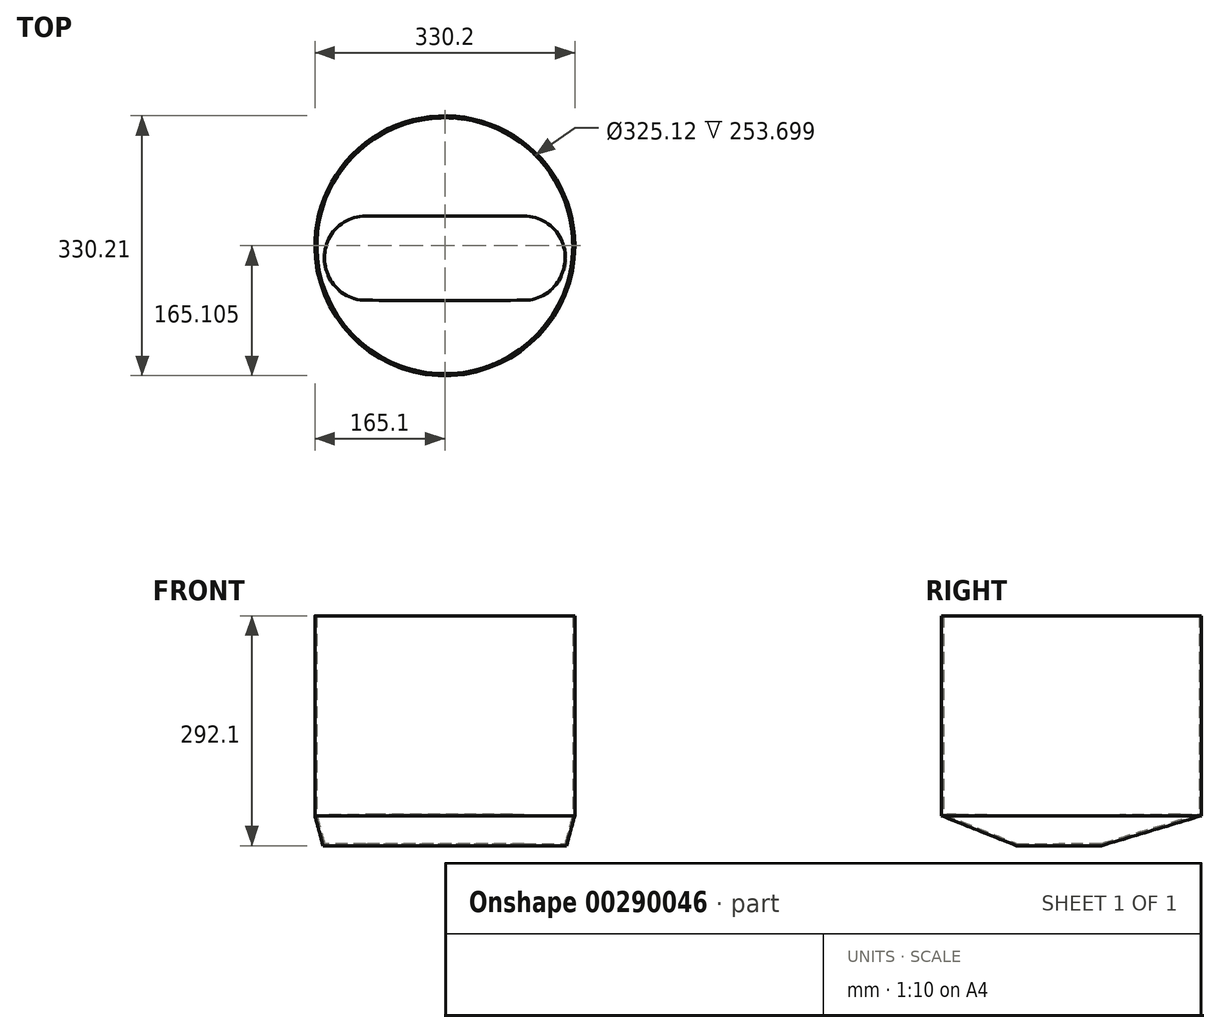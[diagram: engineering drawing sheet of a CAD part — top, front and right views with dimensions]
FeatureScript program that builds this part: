
annotation { "Feature Type Name" : "Feature", "Feature Type Description" : "" }
export const myFeature = defineFeature(function(context is Context, id is Id, definition is map)
    precondition{}
    {
        {
            var Q0;
            Q0=qCreatedBy(makeId("Top.planeOp"),FACE);
            var sketch = newSketch(context, id + "F0", { "sketchPlane" : qUnion([Q0])});
            skArc(sketch, "E0", {"start": v(-100.81, 53.98) * mm, "mid": v(-154.79, 0) * mm, "end": v(-100.81, -53.98) * mm});
            skArc(sketch, "E1", {"start": v(100.8, -53.98) * mm, "mid": v(154.77, 0) * mm, "end": v(100.8, 53.97) * mm});
            skLineSegment(sketch, "E2", {"start": v(-100.81, 53.98) * mm, "end": v(100.8, 53.98) * mm});
            skLineSegment(sketch, "E3", {"start": v(-100.81, -53.98) * mm, "end": v(100.8, -53.98) * mm});
            skSolve(sketch);
        }
        {
            var Q0;
            Q0=qCreatedBy(makeId("Top.planeOp"),FACE);
            cPlane(context, id + "F1", {"entities" : qUnion([Q0]), "cplaneType" : CPlaneType.OFFSET, "offset" : 38.1 * mm, "width" : 152.4 * mm, "height" : 152.4 * mm});
        }
        {
            var Q0;
            Q0=qCreatedBy(id+"F1.planeOp",FACE);
            var sketch = newSketch(context, id + "F2", { "sketchPlane" : qUnion([Q0])});
            skCircle(sketch, "E4", {"center": v(0, 15.88) * mm, "radius": 165.1 * mm});
            skPoint(sketch, "E5", {"position": v(164.34, 0) * mm});
            skPoint(sketch, "E6", {"position": v(-164.34, 0) * mm});
            skSolve(sketch);
        }
        {
            var Q0;
            Q0=qCreatedBy(makeId("Front.planeOp"),FACE);
            var sketch = newSketch(context, id + "F3", { "sketchPlane" : qUnion([Q0])});
            skLineSegment(sketch, "E7", {"start": v(154.77, 0) * mm, "end": v(164.34, 38.1) * mm});
            skSolve(sketch);
        }
        {
            var Q0;
            Q0=qCreatedBy(makeId("Front.planeOp"),FACE);
            var sketch = newSketch(context, id + "F4", { "sketchPlane" : qUnion([Q0])});
            skLineSegment(sketch, "E8", {"start": v(-164.34, 38.1) * mm, "end": v(-154.79, 0) * mm});
            skSolve(sketch);
        }
        {
            var Q0;
            Q0 = qSketchRegion(id + "F0", true);
            var Q1;
            Q1 = qSketchRegion(id + "F2", true);
            var Q2;
            Q2 = qConstructionFilter(qBodyType(qCreatedBy(id + "F3" ,EDGE), BodyType.WIRE), ConstructionObject.NO);
            var Q3;
            Q3 = qConstructionFilter(qBodyType(qCreatedBy(id + "F4" ,EDGE), BodyType.WIRE), ConstructionObject.NO);
            loft(context, id + "F5", {"addGuides" : true, "sheetProfilesArray" : [{ "sheetProfileEntities" : qUnion([Q0]) }, { "sheetProfileEntities" : qUnion([Q1]) }], "guidesArray" : [{ "guideEntities" : qUnion([Q2]), "guideDerivativeType" : LoftGuideDerivativeType.DEFAULT, "guideDerivativeMagnitude" : 1 }, { "guideEntities" : qUnion([Q3]), "guideDerivativeType" : LoftGuideDerivativeType.DEFAULT, "guideDerivativeMagnitude" : 1 }]});
        }
        {
            var Q0;
            Q0 = qSketchRegion(id + "F2", true);
            extrude(context, id + "F6", {"entities" : qUnion([Q0]), "operationType" : NewBodyOperationType.ADD, "depth" : 254 * mm});
        }
        {
            var Q0;
            Q0=makeQuery(id+"F6.opExtrude","CAP_FACE",FACE,{"disambiguationData":[OSD([sQuery(id+"F2.wireOp",EDGE,"E4")])],"isStart":false});
            shell(context, id + "F7", {"entities" : qUnion([Q0]), "thickness" : 2.54 * mm});
        }
    });
